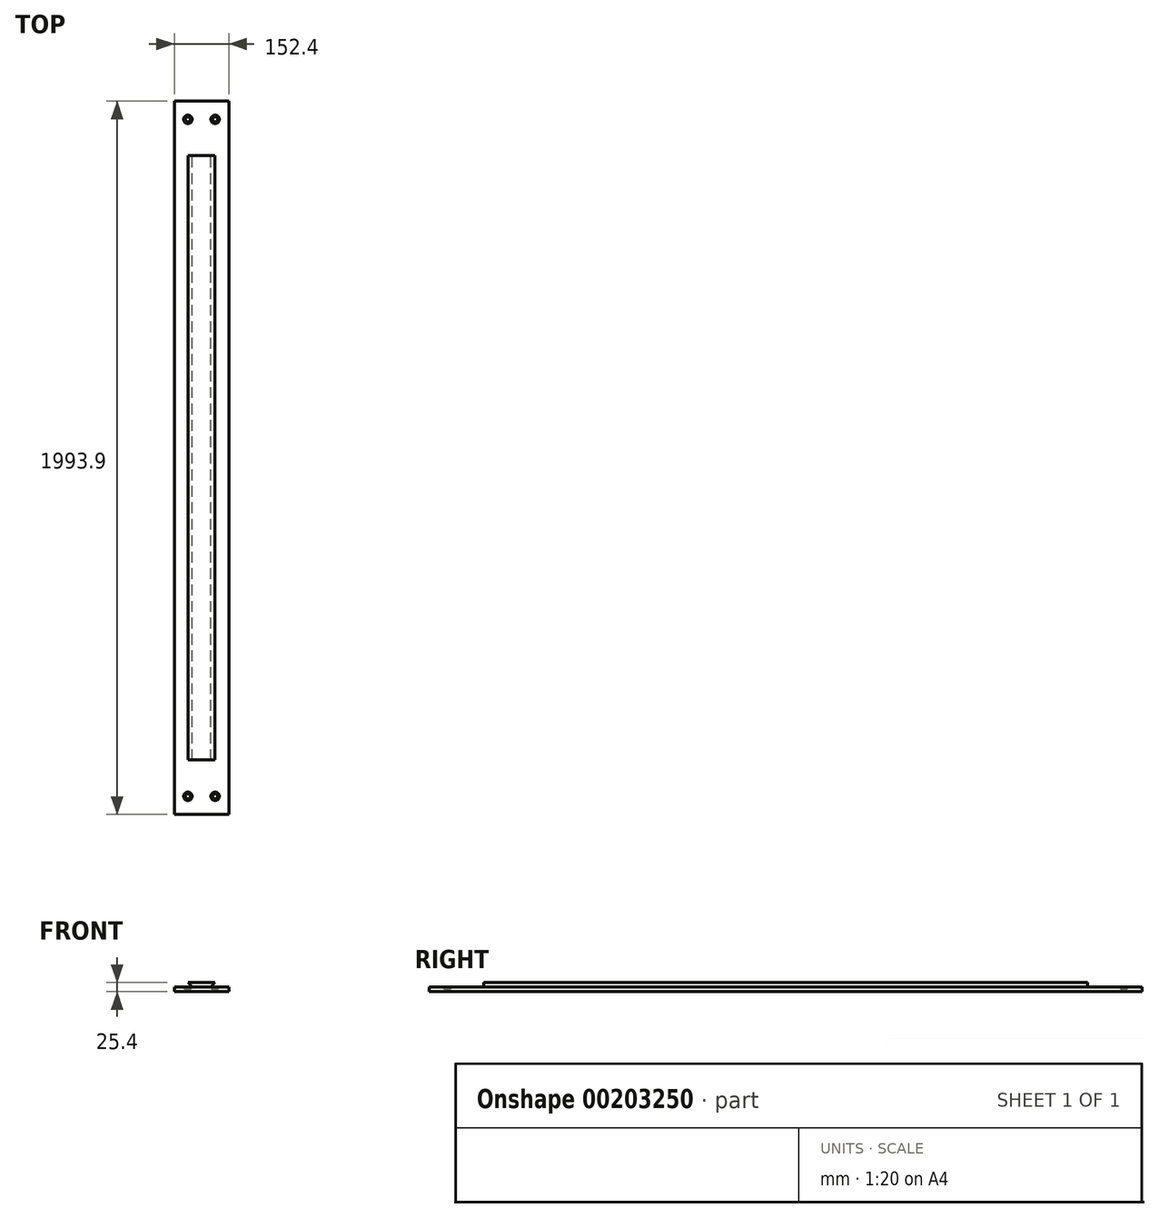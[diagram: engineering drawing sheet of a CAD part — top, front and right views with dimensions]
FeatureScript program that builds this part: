
annotation { "Feature Type Name" : "Feature", "Feature Type Description" : "" }
export const myFeature = defineFeature(function(context is Context, id is Id, definition is map)
    precondition{}
    {
        {
            var Q0;
            Q0=qCreatedBy(makeId("Front.planeOp"),FACE);
            var sketch = newSketch(context, id + "F0", { "sketchPlane" : qUnion([Q0])});
            skLineSegment(sketch, "E0", {"start": v(0, 0) * mm, "end": v(152.4, 0) * mm});
            skLineSegment(sketch, "E1", {"start": v(152.4, 0) * mm, "end": v(152.4, 12.7) * mm});
            skLineSegment(sketch, "E2", {"start": v(152.4, 12.7) * mm, "end": v(101.6, 12.7) * mm});
            skLineSegment(sketch, "E3", {"start": v(101.6, 12.7) * mm, "end": v(114.3, 25.4) * mm});
            skLineSegment(sketch, "E4", {"start": v(114.3, 25.4) * mm, "end": v(38.1, 25.4) * mm});
            skLineSegment(sketch, "E5", {"start": v(38.1, 25.4) * mm, "end": v(50.8, 12.7) * mm});
            skLineSegment(sketch, "E6", {"start": v(50.8, 12.7) * mm, "end": v(0, 12.7) * mm});
            skLineSegment(sketch, "E7", {"start": v(0, 12.7) * mm, "end": v(0, 0) * mm});
            skSolve(sketch);
        }
        {
            var Q0;
            Q0 = qSketchRegion(id + "F0", true);
            extrude(context, id + "F1", {"entities" : qUnion([Q0]), "depth" : 1993.9 * mm});
        }
        {
            var Q0;
            Q0=makeQuery(id+"F1.opExtrude","SWEPT_FACE",FACE,{"disambiguationData":[OSD([sQuery(id+"F0.wireOp",EDGE,"E4")])]});
            var sketch = newSketch(context, id + "F2", { "sketchPlane" : qUnion([Q0])});
            skLineSegment(sketch, "E8.bottom", {"start": v(0, 0) * mm, "end": v(152.4, 0) * mm});
            skLineSegment(sketch, "E8.top", {"start": v(0, -152.4) * mm, "end": v(152.4, -152.4) * mm});
            skLineSegment(sketch, "E8.left", {"start": v(0, 0) * mm, "end": v(0, -152.4) * mm});
            skLineSegment(sketch, "E8.right", {"start": v(152.4, 0) * mm, "end": v(152.4, -152.4) * mm});
            skLineSegment(sketch, "E9", {"start": v(0, -996.95) * mm, "end": v(294.53, -996.95) * mm, "construction": true});
            skLineSegment(sketch, "E10.MirrorCS", {"start": v(152.4, -1993.9) * mm, "end": v(152.4, -1841.5) * mm});
            skLineSegment(sketch, "E11.MirrorCS", {"start": v(0, -1993.9) * mm, "end": v(0, -1841.5) * mm});
            skLineSegment(sketch, "E12.MirrorCS", {"start": v(0, -1841.5) * mm, "end": v(152.4, -1841.5) * mm});
            skLineSegment(sketch, "E13.MirrorCS", {"start": v(0, -1993.9) * mm, "end": v(152.4, -1993.9) * mm});
            skSolve(sketch);
        }
        {
            var Q0;
            Q0 = qSketchRegion(id + "F2", true);
            var Q1;
            Q1=makeQuery(id+"F1.opExtrude","SWEPT_FACE",FACE,{"disambiguationData":[OSD([sQuery(id+"F0.wireOp",EDGE,"E6")])]});
            extrude(context, id + "F3", {"entities" : qUnion([Q0]), "operationType" : NewBodyOperationType.REMOVE, "endBound" : BoundingType.UP_TO_SURFACE, "oppositeDirection" : true, "endBoundEntityFace" : qUnion([Q1]), "depth" : 25.4 * mm});
        }
        {
            var Q0;
            {var subQ0=sQuery(id+"F0.wireOp",EDGE,"E6");Q0=makeQuery(id+"F3.boolean.opBoolean","MERGE",FACE,{"derivedFrom":[makeQuery(id+"F1.opExtrude","SWEPT_FACE",FACE,{"disambiguationData":[OSD([sQuery(id+"F0.wireOp",EDGE,"E2")])]}),makeQuery(id+"F1.opExtrude","SWEPT_FACE",FACE,{"disambiguationData":[OSD([subQ0])]}),makeQuery(id+"F3.opExtrude","CAP_FACE",FACE,{"disambiguationData":[OSD([subQ0]),ownerDisambiguation([makeQuery(id+"F3.opExtrude","SWEPT_BODY",BODY,{"disambiguationData":[OSD([sQuery(id+"F2.wireOp",EDGE,"E8.bottom"),sQuery(id+"F2.wireOp",EDGE,"E8.top"),sQuery(id+"F2.wireOp",EDGE,"E8.left"),sQuery(id+"F2.wireOp",EDGE,"E8.right")])]})])],"isStart":false}),makeQuery(id+"F3.opExtrude","CAP_FACE",FACE,{"disambiguationData":[OSD([subQ0]),ownerDisambiguation([makeQuery(id+"F3.opExtrude","SWEPT_BODY",BODY,{"disambiguationData":[OSD([sQuery(id+"F2.wireOp",EDGE,"E10.MirrorCS"),sQuery(id+"F2.wireOp",EDGE,"E11.MirrorCS"),sQuery(id+"F2.wireOp",EDGE,"E12.MirrorCS"),sQuery(id+"F2.wireOp",EDGE,"E13.MirrorCS")])]})])],"isStart":false})]});}
            var sketch = newSketch(context, id + "F4", { "sketchPlane" : qUnion([Q0])});
            skPoint(sketch, "E14", {"position": v(38.1, -50.8) * mm});
            skPoint(sketch, "E15", {"position": v(114.3, -50.8) * mm});
            skLineSegment(sketch, "E16", {"start": v(0, -996.95) * mm, "end": v(152.4, -996.95) * mm, "construction": true});
            skPoint(sketch, "E17.MirrorP", {"position": v(114.3, -1943.1) * mm});
            skPoint(sketch, "E18.MirrorP", {"position": v(38.1, -1943.1) * mm});
            skSolve(sketch);
        }
        {
            var Q0;
            Q0=sQuery(id+"F4.wireOp",VERTEX,"E14");
            var Q1;
            Q1=sQuery(id+"F4.wireOp",VERTEX,"E15");
            var Q2;
            Q2=sQuery(id+"F4.wireOp",VERTEX,"E18.MirrorP");
            var Q3;
            Q3=sQuery(id+"F4.wireOp",VERTEX,"E17.MirrorP");
            var Q4;
            Q4=makeQuery(id+"F1.opExtrude","SWEPT_BODY",BODY,{"disambiguationData":[OSD([sQuery(id+"F0.wireOp",EDGE,"E0"),sQuery(id+"F0.wireOp",EDGE,"E1"),sQuery(id+"F0.wireOp",EDGE,"E2"),sQuery(id+"F0.wireOp",EDGE,"E3"),sQuery(id+"F0.wireOp",EDGE,"E4"),sQuery(id+"F0.wireOp",EDGE,"E5"),sQuery(id+"F0.wireOp",EDGE,"E6"),sQuery(id+"F0.wireOp",EDGE,"E7")])]});
            hole(context, id + "F5", {"style" : HoleStyle.C_SINK, "endStyle" : HoleEndStyle.THROUGH, "standardTappedOrClearance" : lookupTablePath({ "standard" : "ANSI", "fit" : "Normal (ASME)", "size" : "1/2", "type" : "Clearance" }), "standardBlindInLast" : lookupTablePath({ "fit" : "Free", "standard" : "ANSI", "size" : "1/2", "type" : "Clearance" }), "holeDiameter" : 13.5 * mm, "cSinkDiameter" : 23.83 * mm, "cSinkAngle" : 82 * degree, "startFromSketch" : true, "locations" : qUnion([Q0, Q1, Q2, Q3]), "scope" : qUnion([Q4]), "isTappedThrough" : true});
        }
    });
